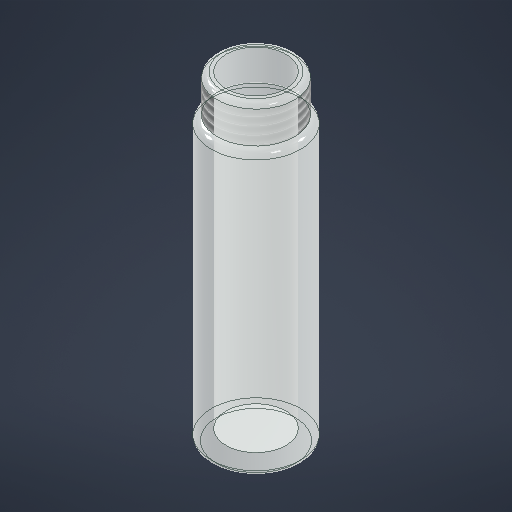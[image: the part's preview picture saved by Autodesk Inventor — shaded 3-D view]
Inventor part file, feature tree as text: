
AUTODESK INVENTOR PART (.ipt)
format: ipt  version: 2025.1 (Build 291241000, 241)  size: 233,984 bytes
history: native  units: mm
features: extrude x4, sketch x4, fillet x2, thread x1
ambient origin geometry x8: Origin, YZ Plane, XZ Plane, XY Plane, X Axis, Y Axis, Z Axis, Center Point
bodies: Solid1 (feature_tree)
feature tree (11):
  extrude  "Extrusion1"  Depth=53.0mm
  extrude  "Extrusion2"  Depth=10.0mm TaperAngle=0.0deg
  fillet  "Fillet1"  Radius=1.5mm
  thread  "Thread1"  [1 undecoded]
  extrude  "Extrusion3"  Depth=58.0mm TaperAngle=0.0deg
  fillet  "Fillet2"  Radius=1.0mm
  extrude  "Extrusion4"  Depth=50.0mm TaperAngle=0.0deg
  sketch  "Sketch1"  dims[d0=53.0mm d1=0.0mm d2=16.8mm]
  sketch  "Sketch2"  dims[d3=14.5mm d4=7.0mm d5=0.0mm d6=1.5mm d7=10.0mm d8=0.0mm]
  sketch  "Sketch3"  dims[d9=11.25mm d10=58.0mm d11=0.0mm d12=1.0mm]
  sketch  "Sketch4"  dims[d13=18.0mm d14=50.0mm d15=0.0mm d16=0.0mm d17=0.0mm d18=0.0mm d19=0.0mm]
note: 1 required parameter value undecoded (feature->parameter linkage not recoverable at this tier; creation-order binding heuristic only, values carry confidence <= 0.55)
